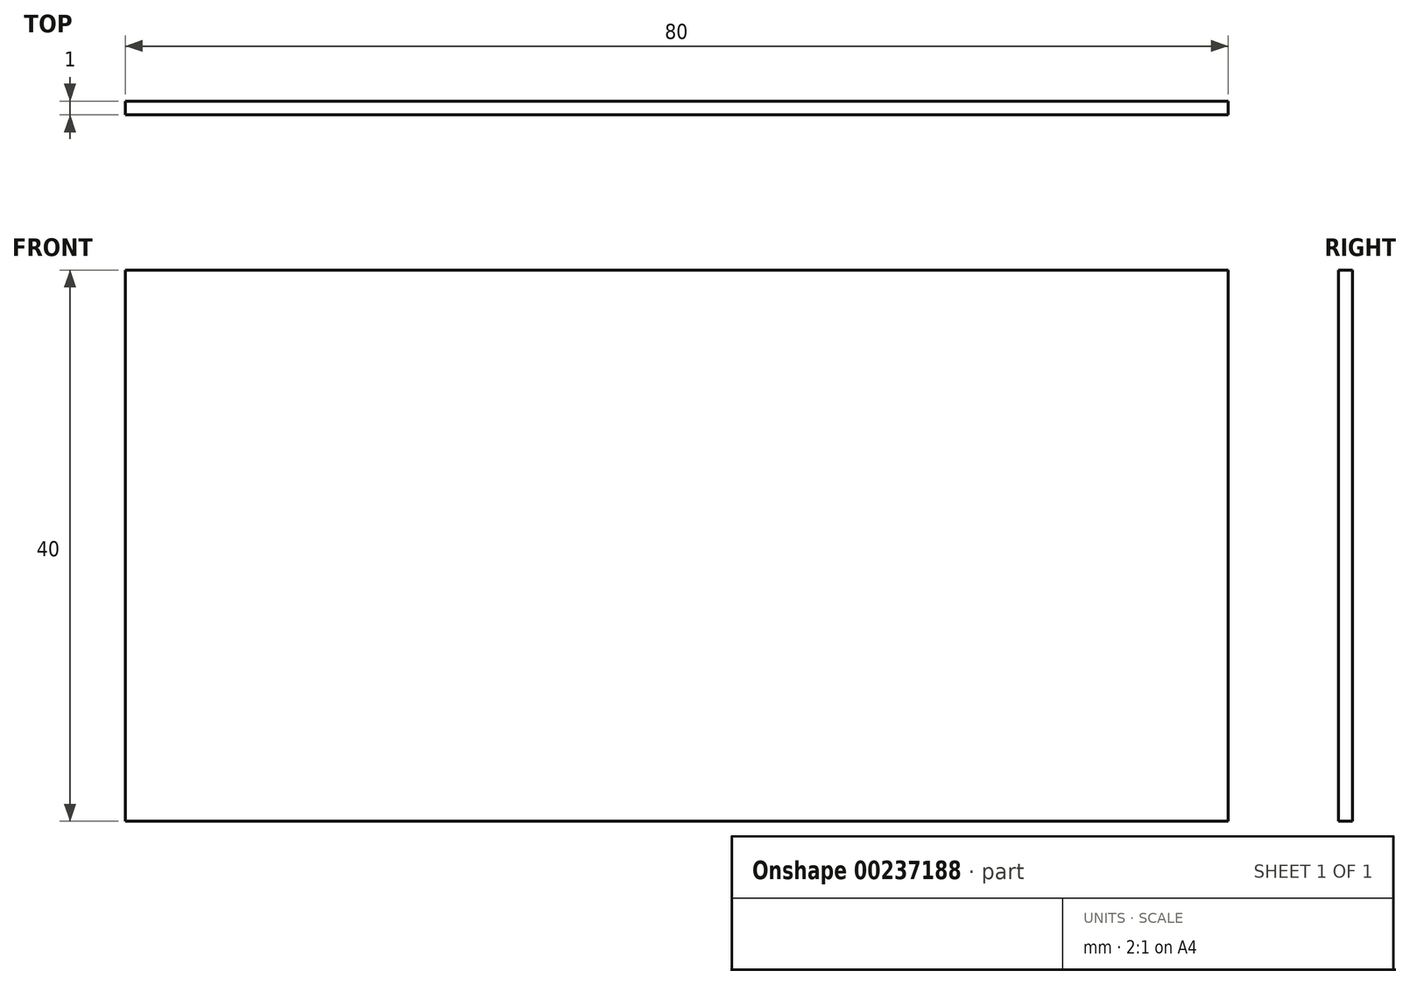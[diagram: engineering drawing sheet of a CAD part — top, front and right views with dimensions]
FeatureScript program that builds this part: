
annotation { "Feature Type Name" : "Feature", "Feature Type Description" : "" }
export const myFeature = defineFeature(function(context is Context, id is Id, definition is map)
    precondition{}
    {
        {
            var Q0;
            Q0=qCreatedBy(makeId("Front.planeOp"),FACE);
            var sketch = newSketch(context, id + "F0", { "sketchPlane" : qUnion([Q0])});
            skLineSegment(sketch, "E0.bottom", {"start": v(-40, 20) * mm, "end": v(40, 20) * mm});
            skLineSegment(sketch, "E0.top", {"start": v(-40, -20) * mm, "end": v(40, -20) * mm});
            skLineSegment(sketch, "E0.left", {"start": v(-40, 20) * mm, "end": v(-40, -20) * mm});
            skLineSegment(sketch, "E0.right", {"start": v(40, 20) * mm, "end": v(40, -20) * mm});
            skPoint(sketch, "E0.middle", {"position": v(0, 0) * mm});
            skSolve(sketch);
        }
        {
            var Q0;
            Q0=makeQuery(id+"F0.imprint","IMPRINT",FACE,{"disambiguationData":[TD([[makeQuery(id+"F0.imprint","IMPRINT",EDGE,{"derivedFrom":sQuery(id+"F0.wireOp",EDGE,"E0.bottom")}),-1.0]])]});
            extrude(context, id + "F1", {"entities" : qUnion([Q0]), "depth" : 1 * mm});
        }
    });
